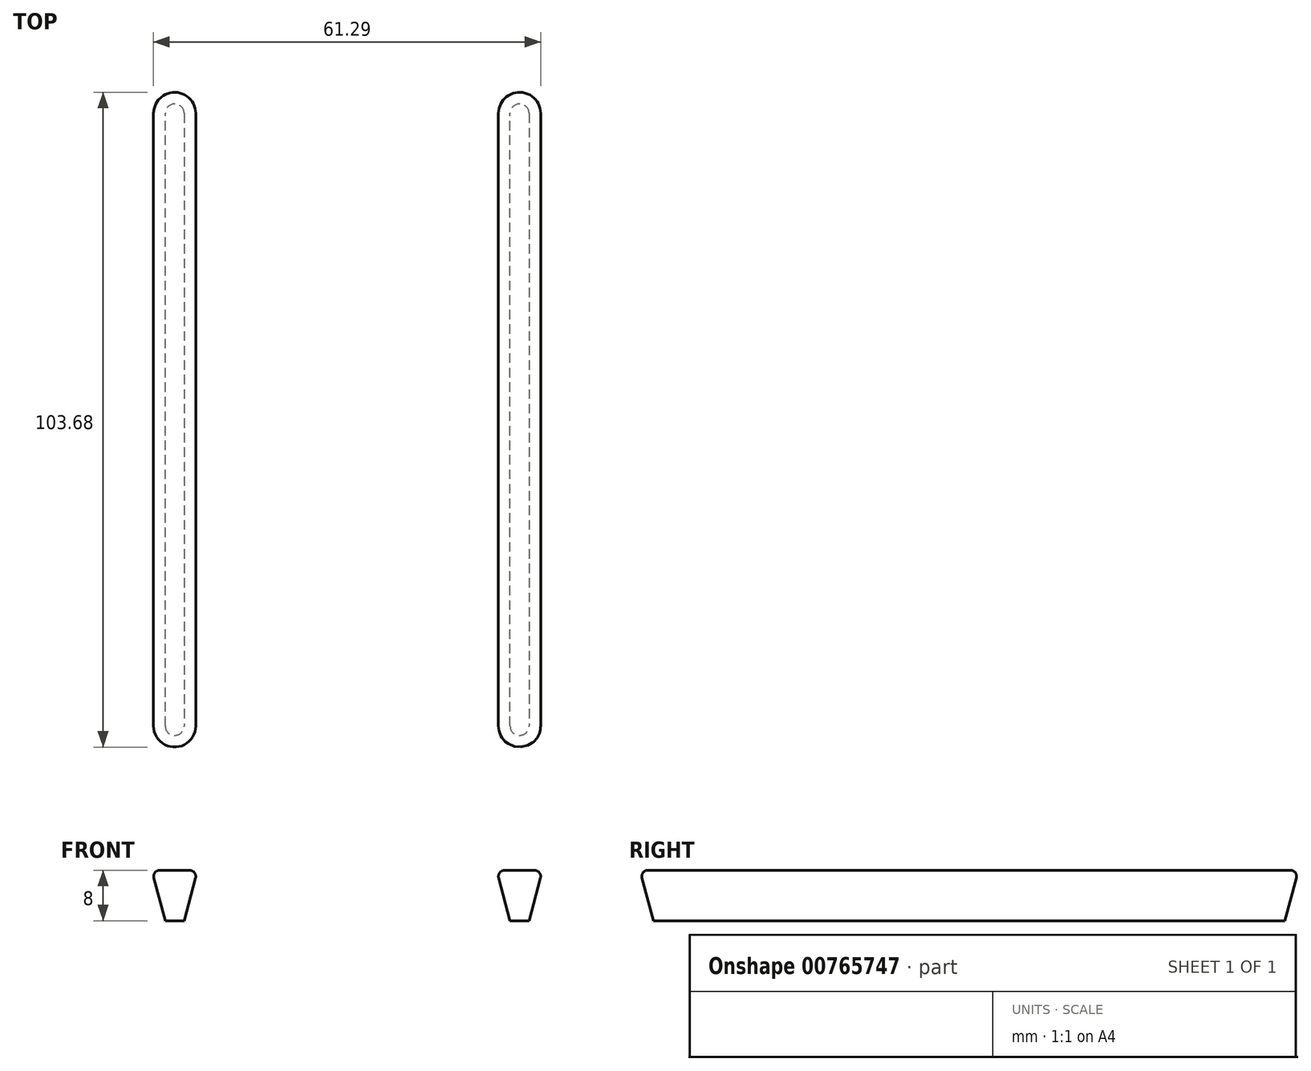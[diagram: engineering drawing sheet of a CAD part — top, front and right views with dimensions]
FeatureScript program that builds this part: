
annotation { "Feature Type Name" : "Feature", "Feature Type Description" : "" }
export const myFeature = defineFeature(function(context is Context, id is Id, definition is map)
    precondition{}
    {
        {
            var Q0;
            Q0=qCreatedBy(makeId("Top.planeOp"),FACE);
            var sketch = newSketch(context, id + "F0", { "sketchPlane" : qUnion([Q0])});
            skLineSegment(sketch, "E0", {"start": v(-65.17, 1.5) * mm, "end": v(-65.17, 98.5) * mm});
            skLineSegment(sketch, "E1", {"start": v(-10.56, 1.5) * mm, "end": v(-10.56, 98.5) * mm});
            skLineSegment(sketch, "E2", {"start": v(-12.06, 0) * mm, "end": v(-12.06, 0) * mm});
            skLineSegment(sketch, "E3", {"start": v(-12.06, 100) * mm, "end": v(-12.06, 100) * mm});
            skLineSegment(sketch, "E4", {"start": v(-66.67, 100) * mm, "end": v(-66.67, 100) * mm});
            skLineSegment(sketch, "E5", {"start": v(-66.67, 0) * mm, "end": v(-66.67, 0) * mm});
            skLineSegment(sketch, "E6", {"start": v(-68.17, 98.5) * mm, "end": v(-68.17, 1.5) * mm});
            skLineSegment(sketch, "E7", {"start": v(-13.56, 98.5) * mm, "end": v(-13.56, 1.5) * mm});
            skPoint(sketch, "E8.visualSharp", {"position": v(-10.56, 100) * mm});
            skArc(sketch, "E8.filletArc", {"start": v(-10.56, 99.5) * mm, "mid": v(-10.71, 99.85) * mm, "end": v(-11.06, 100) * mm});
            skPoint(sketch, "E9.visualSharp", {"position": v(-13.56, 100) * mm});
            skArc(sketch, "E9.filletArc", {"start": v(-13.06, 100) * mm, "mid": v(-13.42, 99.85) * mm, "end": v(-13.56, 99.5) * mm});
            skArc(sketch, "E10.filletArc", {"start": v(-10.56, 99.7) * mm, "mid": v(-10.65, 99.91) * mm, "end": v(-10.86, 100) * mm});
            skArc(sketch, "E11.filletArc", {"start": v(-10.56, 98.5) * mm, "mid": v(-11, 99.56) * mm, "end": v(-12.06, 100) * mm});
            skArc(sketch, "E12.filletArc", {"start": v(-12.06, 100) * mm, "mid": v(-13.12, 99.56) * mm, "end": v(-13.56, 98.5) * mm});
            skPoint(sketch, "E13.visualSharp", {"position": v(-65.17, 100) * mm});
            skArc(sketch, "E13.filletArc", {"start": v(-65.17, 98.5) * mm, "mid": v(-65.6, 99.56) * mm, "end": v(-66.67, 100) * mm});
            skPoint(sketch, "E14.visualSharp", {"position": v(-68.17, 100) * mm});
            skArc(sketch, "E14.filletArc", {"start": v(-66.67, 100) * mm, "mid": v(-67.73, 99.56) * mm, "end": v(-68.17, 98.5) * mm});
            skPoint(sketch, "E15.visualSharp", {"position": v(-68.17, 0) * mm});
            skArc(sketch, "E15.filletArc", {"start": v(-68.17, 1.5) * mm, "mid": v(-67.73, 0.44) * mm, "end": v(-66.67, 0) * mm});
            skPoint(sketch, "E16.visualSharp", {"position": v(-65.17, 0) * mm});
            skArc(sketch, "E16.filletArc", {"start": v(-66.67, 0) * mm, "mid": v(-65.6, 0.44) * mm, "end": v(-65.17, 1.5) * mm});
            skPoint(sketch, "E17.visualSharp", {"position": v(-13.56, 0) * mm});
            skArc(sketch, "E17.filletArc", {"start": v(-13.56, 1.5) * mm, "mid": v(-13.12, 0.44) * mm, "end": v(-12.06, 0) * mm});
            skPoint(sketch, "E18.visualSharp", {"position": v(-10.56, 0) * mm});
            skArc(sketch, "E18.filletArc", {"start": v(-12.06, 0) * mm, "mid": v(-11, 0.44) * mm, "end": v(-10.56, 1.5) * mm});
            skSolve(sketch);
        }
        {
            var Q0;
            Q0=makeQuery(id+"F0.imprint","IMPRINT",FACE,{"disambiguationData":[TD([[makeQuery(id+"F0.imprint","IMPRINT",EDGE,{"derivedFrom":sQuery(id+"F0.wireOp",EDGE,"E1")}),1.0]])]});
            extrude(context, id + "F1", {"entities" : qUnion([Q0]), "depth" : 8 * mm, "offsetDistance" : 25 * mm, "hasDraft" : true, "draftAngle" : 15 * degree});
        }
        {
            var Q0;
            Q0=makeQuery(id+"F0.imprint","IMPRINT",FACE,{"disambiguationData":[TD([[makeQuery(id+"F0.imprint","IMPRINT",EDGE,{"derivedFrom":sQuery(id+"F0.wireOp",EDGE,"E0")}),1.0]])]});
            extrude(context, id + "F2", {"entities" : qUnion([Q0]), "depth" : 8 * mm, "offsetDistance" : 25 * mm, "hasDraft" : true, "draftAngle" : 15 * degree});
        }
        {
            var Q0;
            Q0=makeQuery(id+"F2.opExtrude","CAP_FACE",FACE,{"disambiguationData":[OSD([sQuery(id+"F0.wireOp",EDGE,"E0"),sQuery(id+"F0.wireOp",EDGE,"E6"),sQuery(id+"F0.wireOp",EDGE,"E13.filletArc"),sQuery(id+"F0.wireOp",EDGE,"E14.filletArc"),sQuery(id+"F0.wireOp",EDGE,"E15.filletArc"),sQuery(id+"F0.wireOp",EDGE,"E16.filletArc")])],"isStart":false});
            var Q1;
            Q1=makeQuery(id+"F1.opExtrude","CAP_FACE",FACE,{"disambiguationData":[OSD([sQuery(id+"F0.wireOp",EDGE,"E1"),sQuery(id+"F0.wireOp",EDGE,"E7"),sQuery(id+"F0.wireOp",EDGE,"E11.filletArc"),sQuery(id+"F0.wireOp",EDGE,"E12.filletArc"),sQuery(id+"F0.wireOp",EDGE,"E17.filletArc"),sQuery(id+"F0.wireOp",EDGE,"E18.filletArc")])],"isStart":false});
            fillet(context, id + "F3", {"entities" : qUnion([Q0, Q1]), "radius" : 1 * mm, "tangentPropagation" : true, "allowEdgeOverflow" : false});
        }
    });
